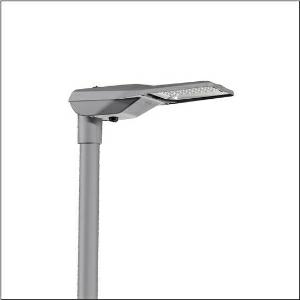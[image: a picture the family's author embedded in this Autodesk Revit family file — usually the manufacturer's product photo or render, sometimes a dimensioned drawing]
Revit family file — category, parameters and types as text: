
# Revit family: streetlight_sl_21_iq_mini___pl52_5xe2h31y08gb_067c
name_source: partatom
category: Lighting Fixtures
units: mm (PartAtom-declared; Revit-internal decimal feet)

## family parameters
Cut with Voids When Loaded = No
Host = Face
Light Source = No
Part Type = Normal
Room Calculation Point = No
Round Connector Dimension = Use Diameter
Shared = No

## types (1)
- --- (1 x LED, 5880 lm, 39.8 W, 3000K)
    Apparent Load = 40 VA
    CIE Flux Codes = 27 59 98 100 100
    Color Rendering = 70
    Color Temperature = 3000K
    Default Elevation = 1800 mm
    Description = Streetlight SL 21 iQ mini, mast luminaire, primary light control with lens, of PMMA, primary optical cover: cover, of toughened safety glass, transparent, light distribution: PL52, light emission: direct distribution, primary light characteristic: asymmetric, installation type: post-top, side-entry, LED, High Power LED, rated luminous flux: 5.880lm, luminous efficacy: 148lm/W, light colour: 730, colour temperature: 3000K, control gear: iQ-Street Remote, D4i with power reduction, control: pre-setting: logarithmic dimming characteristic, Street-Remote, Auto-Match, Temp-Guard, Lumen-Switch, Night-Set, Smart-Wire, Light-Fading, Desk-Remote (wireless, voltage-free reading and setting of iQ features in the workshop via application-optimized NFC function/RFID function), optimised constant luminous flux control (CLO 2.0), mains connection: 220..240V, AC, 50/60Hz, start of lifetime: 40W, end of service life: 41W, reduction: 18W, luminaire housing, of diecast aluminium, powder-coated, Siteco® metallic grey (DB 702S), corrosivity category C5 mid according to DIN EN ISO 12944, please order mast flange separately, inclination adjustable: 0°, 5°, 10°, 15°, sealing non-destructively replaceable, multi-level sealing system, length: 628mm, width: 235mm, height: 110mm, mast flange for spigot size: 42mm (side-entry): 5XC10008XM4, 60/48mm (side-entry/post-top): 5XC10108XM2, 76/60mm (side-entry/post-top): 5XC10108XM1, mounting height: 4..8m, Smart Interface below and above, protection rating (complete): IP66, insulation class (complete): insulation class II (safety insulation), certification: CE, ENEC, ENEC+, VDE, impact resistance: IK10, permissible operating ambient temperature for outdoor applications: -40..+50°C, standard-compliant lighting for roads and squares, packaging unit: 1 piece

Light Distribution: PL52
    Height = 110 mm
    Lamp = 1 x LED
    Lamp Light Flux = 5880 lm
    Lamp Power = 39.8 W
    Lamp count = 1
    Length = 625 mm
    Luminous efficacy = 148 lm/W
    Manufacturer = Siteco
    ModVariant = No
    Model = 5XE2H31Y08GB
    Number of Poles = 1
    OnlyDefault = Yes
    Power Factor = 1
    Product Name = Streetlight SL 21 iQ mini | PL52
    Product group = mast luminaire | pylon top
    ProductGroupID = 6100
    Protection Class = Protection class II
    Protection Degree = IP 66
    RLX_Detail_Level = 1
    RLX_Emergency_Light_Flux = 0 lm
    RLX_Emergency_Type = 0
    RLX_Emergency_Type_DB = No
    RlxData = <blob elided: 102521 chars, md5=6552b9f3>
    Socket = socket
    Standby Power = 0 W
    System Light Flux = 5880 lm
    System Power = 40 W
    Type Comments = factory setting: luminous flux: 100 % | dim-lin: 254 | 800 mA
    Type Image = l_1003514.jpg
    URL = http://relux.com
    VarID = @adj_137427
    Voltage = 0 V
    Weight = 0.00 kg
    Width = 234 mm

## geometry (parser evidence)
native form markers: Blend x4, Sweep x10
no freeform markers — native parametric forms only
